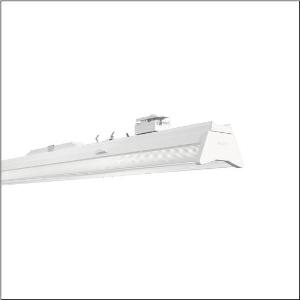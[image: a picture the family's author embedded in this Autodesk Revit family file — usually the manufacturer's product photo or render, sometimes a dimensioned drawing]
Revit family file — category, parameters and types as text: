
# Revit family: licross_r__21_performance_mo_52td16dn66xg_64f4
name_source: partatom
category: Lighting Fixtures
units: mm (PartAtom-declared; Revit-internal decimal feet)

## family parameters
Cut with Voids When Loaded = No
Host = Face
Light Source = No
Part Type = Normal
Room Calculation Point = No
Round Connector Dimension = Use Diameter
Shared = No

## types (1)
- --- (1 x LED, 6000 lm, 33.8 W, 6500K)
    Apparent Load = 34 VA
    CIE Flux Codes = 66 88 96 79 100
    Color Rendering = 80
    Color Temperature = 6500K
    Default Elevation = 1800 mm
    Description = Licross® 21 Performance MO, luminaire insert, of sheet steel, galvanised, coil coated, white, length: 1.500mm, width: 120mm, height: 123mm, LED rated luminous flux: 6.000lm, light colour: 865, SDCM (Standard Deviation of Colour Matching)MacAdam ≤ 3 SDCM (initial), control gear: DALI 2, with plug, 5-pole, with phase selection, mains connection: 220..240V, AC, 50/60Hz, rated input power: 34W, internal wiring halogen-free, primary light control with lens, of plastic, primary optical cover: cover, of PMMA, light emission: direct/indirect distribution, primary light characteristic: symmetric, protection rating (complete): IP54, insulation class (complete): insulation class I (protective earthing), certification: CE, ENEC, VDE, UKCA, protection symbol: D if used in an environment with non-conductive dust loads with corresponding accessories, impact resistance: IK06, permissible ambient temperature for indoor applications: -25..+45°C, corresponds to IFS (International Featured Standards) requirements for safety and quality in the food industry, reducing of maximum allowable ambient temperature of 5°C with ceiling mounting, LABS conformity tested according to VDMA 24364:2018-05, packaging unit: 1 piece
    Height = 114 mm
    Lamp = 1 x LED
    Lamp Light Flux = 6000 lm
    Lamp Power = 33.8 W
    Lamp count = 1
    Length = 1500 mm
    Luminous efficacy = 178 lm/W
    Manufacturer = Siteco
    ModVariant = No
    Model = 52TD16DN66XG
    Mounting Place = Ceiling
    Mounting Type = Pendant
    Number of Poles = 1
    OnlyDefault = Yes
    Power Factor = 1
    Product Name = Licross® 21 Performance MO
    Product group = luminaire insert | ceiling pendant
    ProductGroupID = 901
    Protection Class = Protection class I
    Protection Degree = IP 54
    RLX_Detail_Level = 1
    RLX_Emergency_Light_Flux = 0 lm
    RLX_Emergency_Type = 0
    RLX_Emergency_Type_DB = No
    RlxData = <blob elided: 33817 chars, md5=0acac749>
    Socket = socket
    Standby Power = 0 W
    System Light Flux = 6000 lm
    System Power = 34 W
    Type Comments = factory setting: luminous flux: 100 % | dim-lin: 254 | 229 mA
    Type Image = l_1256138.jpg
    URL = http://relux.com
    VarID = @adj_038045
    Voltage = 0 V
    Weight = 0.00 kg
    Width = 120 mm

## geometry (parser evidence)
native form markers: Blend x4, Sweep x12
no freeform markers — native parametric forms only
